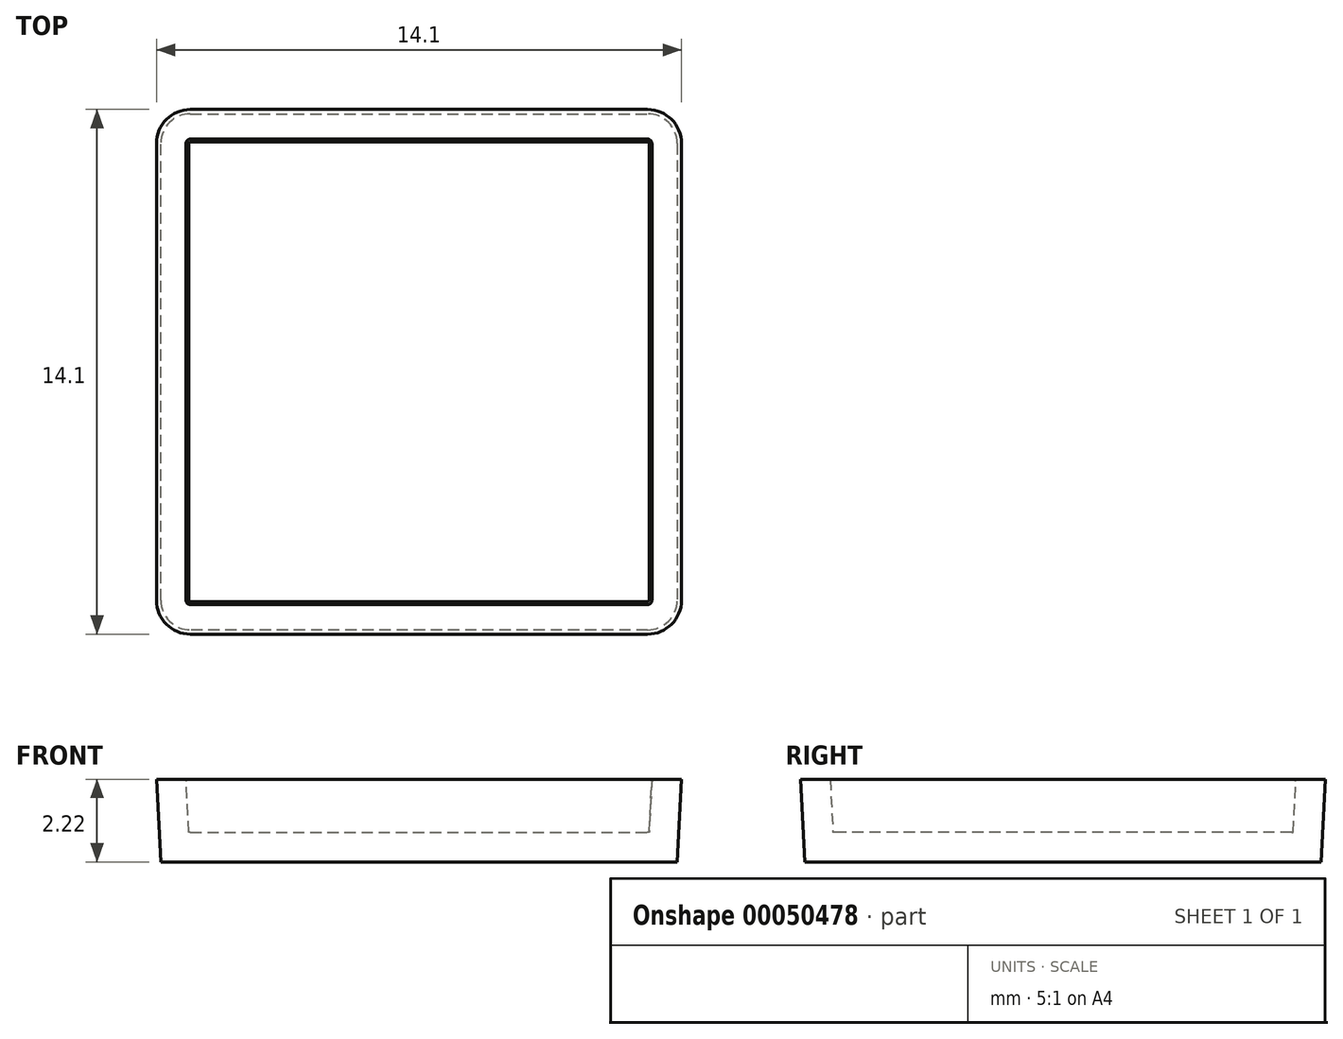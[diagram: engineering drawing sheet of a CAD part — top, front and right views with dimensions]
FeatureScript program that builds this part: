
annotation { "Feature Type Name" : "Feature", "Feature Type Description" : "" }
export const myFeature = defineFeature(function(context is Context, id is Id, definition is map)
    precondition{}
    {
        {
            var Q0;
            Q0=qCreatedBy(makeId("Top.planeOp"),FACE);
            var sketch = newSketch(context, id + "F0", { "sketchPlane" : qUnion([Q0])});
            skLineSegment(sketch, "E0.bottom", {"start": v(6.14, 6.93) * mm, "end": v(-6.14, 6.93) * mm});
            skLineSegment(sketch, "E0.top", {"start": v(6.14, -6.93) * mm, "end": v(-6.14, -6.93) * mm});
            skLineSegment(sketch, "E0.left", {"start": v(6.93, 6.14) * mm, "end": v(6.93, -6.14) * mm});
            skLineSegment(sketch, "E0.right", {"start": v(-6.93, 6.14) * mm, "end": v(-6.93, -6.14) * mm});
            skPoint(sketch, "E0.middle", {"position": v(0, 0) * mm});
            skPoint(sketch, "E1.visualSharp", {"position": v(-6.93, 6.93) * mm});
            skArc(sketch, "E1.filletArc", {"start": v(-6.14, 6.93) * mm, "mid": v(-6.7, 6.7) * mm, "end": v(-6.93, 6.14) * mm});
            skPoint(sketch, "E2.visualSharp", {"position": v(6.93, 6.93) * mm});
            skArc(sketch, "E2.filletArc", {"start": v(6.93, 6.14) * mm, "mid": v(6.7, 6.7) * mm, "end": v(6.14, 6.93) * mm});
            skPoint(sketch, "E3.visualSharp", {"position": v(6.93, -6.93) * mm});
            skArc(sketch, "E3.filletArc", {"start": v(6.14, -6.93) * mm, "mid": v(6.7, -6.7) * mm, "end": v(6.93, -6.14) * mm});
            skPoint(sketch, "E4.visualSharp", {"position": v(-6.93, -6.93) * mm});
            skArc(sketch, "E4.filletArc", {"start": v(-6.93, -6.14) * mm, "mid": v(-6.7, -6.7) * mm, "end": v(-6.14, -6.93) * mm});
            skSolve(sketch);
        }
        {
            var Q0;
            Q0 = qSketchRegion(id + "F0", true);
            extrude(context, id + "F1", {"entities" : qUnion([Q0]), "depth" : 2.22 * mm, "hasDraft" : true, "draftAngle" : 3 * degree});
        }
        {
            var Q0;
            Q0=makeQuery(id+"F1.opExtrude","CAP_FACE",FACE,{"disambiguationData":[OSD([sQuery(id+"F0.wireOp",EDGE,"E0.bottom"),sQuery(id+"F0.wireOp",EDGE,"E0.top"),sQuery(id+"F0.wireOp",EDGE,"E0.left"),sQuery(id+"F0.wireOp",EDGE,"E0.right"),sQuery(id+"F0.wireOp",EDGE,"E1.filletArc"),sQuery(id+"F0.wireOp",EDGE,"E2.filletArc"),sQuery(id+"F0.wireOp",EDGE,"E3.filletArc"),sQuery(id+"F0.wireOp",EDGE,"E4.filletArc")])],"isStart":false});
            shell(context, id + "F2", {"entities" : qUnion([Q0]), "thickness" : 0.8 * mm});
        }
    });
